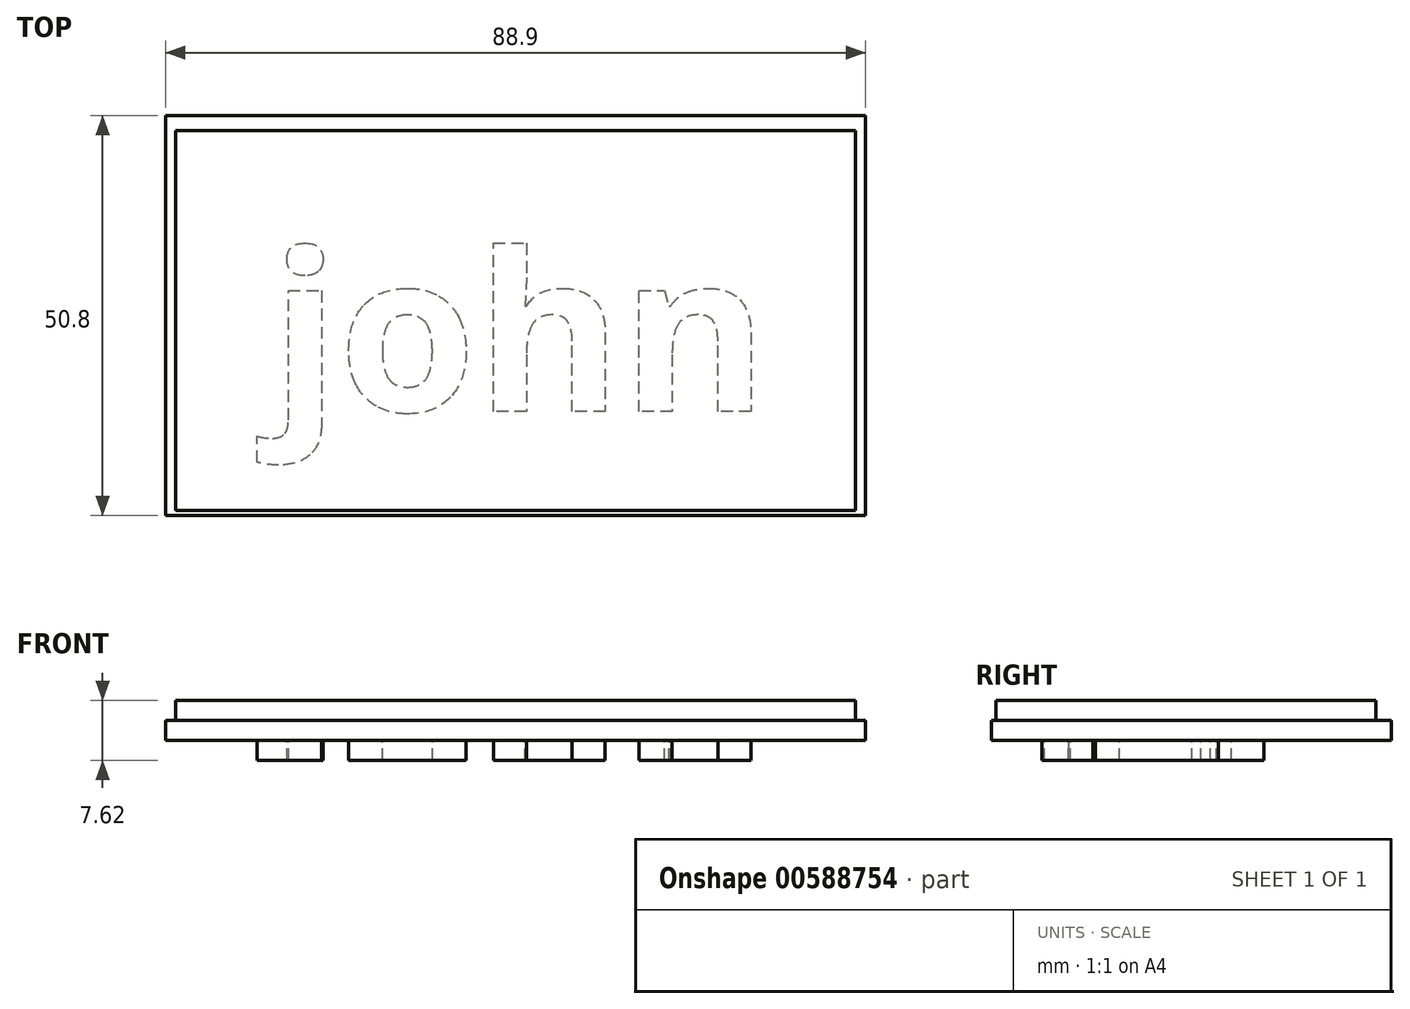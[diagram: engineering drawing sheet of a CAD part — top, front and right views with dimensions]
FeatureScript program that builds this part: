
annotation { "Feature Type Name" : "Feature", "Feature Type Description" : "" }
export const myFeature = defineFeature(function(context is Context, id is Id, definition is map)
    precondition{}
    {
        {
            var Q0;
            Q0=qCreatedBy(makeId("Top.planeOp"),FACE);
            var sketch = newSketch(context, id + "F0", { "sketchPlane" : qUnion([Q0])});
            skLineSegment(sketch, "E0.bottom", {"start": v(-80.8, 31.04) * mm, "end": v(-68.1, 31.04) * mm});
            skLineSegment(sketch, "E0.top", {"start": v(-80.8, -19.76) * mm, "end": v(-68.1, -19.76) * mm});
            skLineSegment(sketch, "E0.left", {"start": v(-80.8, 31.04) * mm, "end": v(-80.8, -19.76) * mm});
            skLineSegment(sketch, "E0.right", {"start": v(-68.1, 31.04) * mm, "end": v(-68.1, -19.76) * mm});
            skLineSegment(sketch, "E1", {"start": v(-68.1, 31.04) * mm, "end": v(-68.1, 31.04) * mm});
            skLineSegment(sketch, "E2.bottom", {"start": v(-68.1, 31.04) * mm, "end": v(8.1, 31.04) * mm});
            skLineSegment(sketch, "E2.top", {"start": v(-68.1, -19.76) * mm, "end": v(8.1, -19.76) * mm});
            skLineSegment(sketch, "E2.right", {"start": v(8.1, 31.04) * mm, "end": v(8.1, -19.76) * mm});
            skSolve(sketch);
        }
        {
            var Q0;
            Q0 = qSketchRegion(id + "F0", true);
            extrude(context, id + "F1", {"entities" : qUnion([Q0]), "depth" : 2.54 * mm, "offsetDistance" : 25.4 * mm});
        }
        {
            var Q0;
            Q0=qCreatedBy(makeId("Top.planeOp"),FACE);
            var sketch = newSketch(context, id + "F2", { "sketchPlane" : qUnion([Q0])});
            skLineSegment(sketch, "E3.bottom", {"start": v(-79.54, 29.1) * mm, "end": v(6.82, 29.1) * mm});
            skLineSegment(sketch, "E3.top", {"start": v(-79.54, -19.16) * mm, "end": v(6.82, -19.16) * mm});
            skLineSegment(sketch, "E3.left", {"start": v(-79.54, 29.1) * mm, "end": v(-79.54, -19.16) * mm});
            skLineSegment(sketch, "E3.right", {"start": v(6.82, 29.1) * mm, "end": v(6.82, -19.16) * mm});
            skSolve(sketch);
        }
        {
            var Q0;
            Q0 = qSketchRegion(id + "F2", true);
            extrude(context, id + "F3", {"entities" : qUnion([Q0]), "operationType" : NewBodyOperationType.ADD, "depth" : 5.08 * mm, "offsetDistance" : 25.4 * mm});
        }
        {
            var Q0;
            Q0=qCreatedBy(makeId("Top.planeOp"),FACE);
            var sketch = newSketch(context, id + "F4", { "sketchPlane" : qUnion([Q0])});
            skText(sketch, "E4", { "text": "john", "fontName": "OpenSans-Bold.ttf"});
            const initialGuessF4  = {"E4": [-0.0674, -0.00658, 1, 0, 0.02028]};
            skSetInitialGuess(sketch, initialGuessF4);
            skSolve(sketch);
        }
        {
            var Q0;
            Q0 = qSketchRegion(id + "F4", true);
            extrude(context, id + "F5", {"entities" : qUnion([Q0]), "operationType" : NewBodyOperationType.ADD, "depth" : -2.54 * mm, "offsetDistance" : 25.4 * mm});
        }
    });
